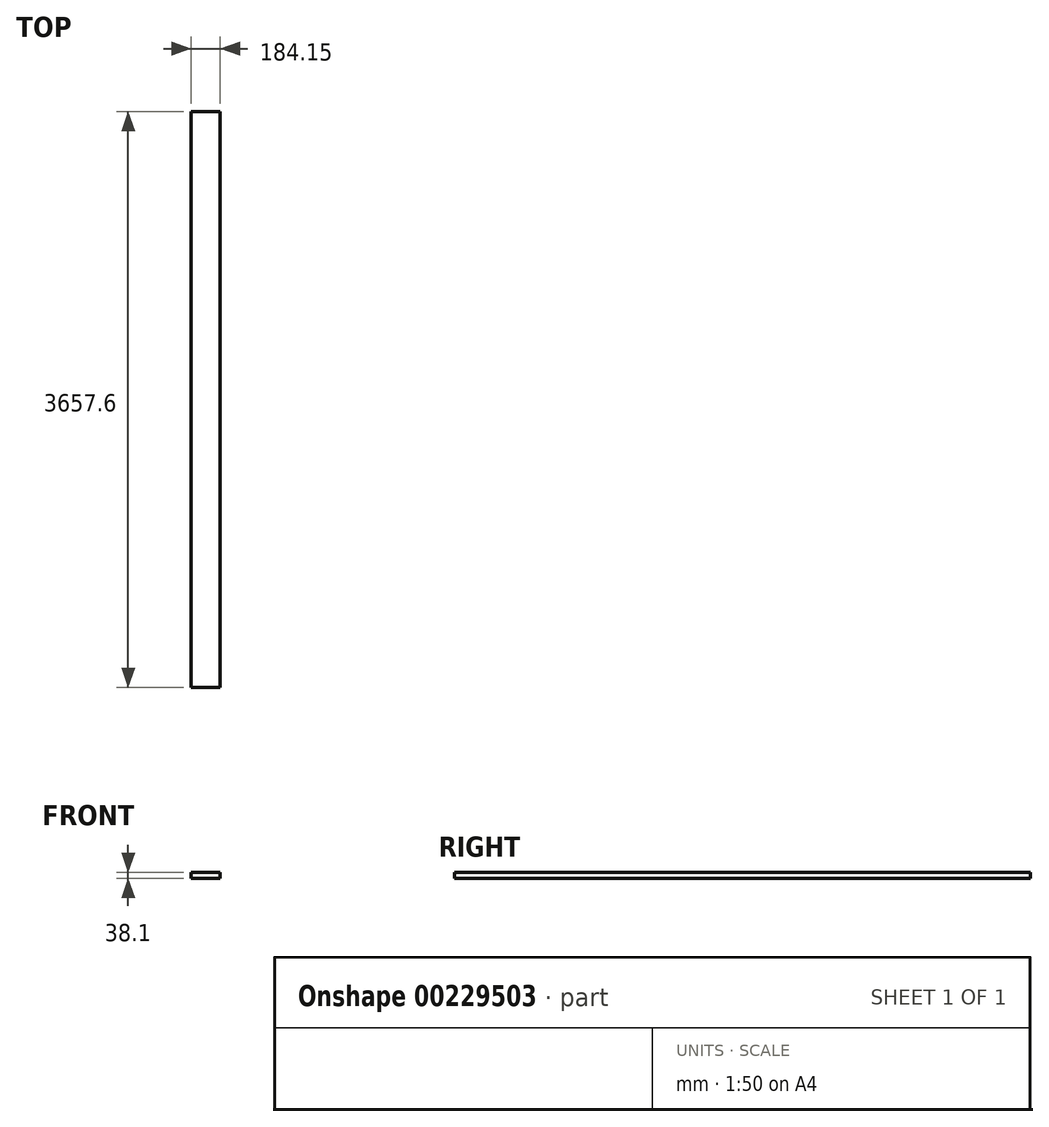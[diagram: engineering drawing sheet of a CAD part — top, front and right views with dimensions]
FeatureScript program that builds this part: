
annotation { "Feature Type Name" : "Feature", "Feature Type Description" : "" }
export const myFeature = defineFeature(function(context is Context, id is Id, definition is map)
    precondition{}
    {
        {
            var Q0;
            Q0=qCreatedBy(makeId("Front.planeOp"),FACE);
            var sketch = newSketch(context, id + "F0", { "sketchPlane" : qUnion([Q0])});
            skLineSegment(sketch, "E0.bottom", {"start": v(0, 0) * mm, "end": v(184.15, 0) * mm});
            skLineSegment(sketch, "E0.top", {"start": v(0, -38.1) * mm, "end": v(184.15, -38.1) * mm});
            skLineSegment(sketch, "E0.left", {"start": v(0, 0) * mm, "end": v(0, -38.1) * mm});
            skLineSegment(sketch, "E0.right", {"start": v(184.15, 0) * mm, "end": v(184.15, -38.1) * mm});
            skSolve(sketch);
        }
        {
            var Q0;
            Q0 = qSketchRegion(id + "F0", true);
            extrude(context, id + "F1", {"entities" : qUnion([Q0]), "depth" : 3657.6 * mm});
        }
    });
